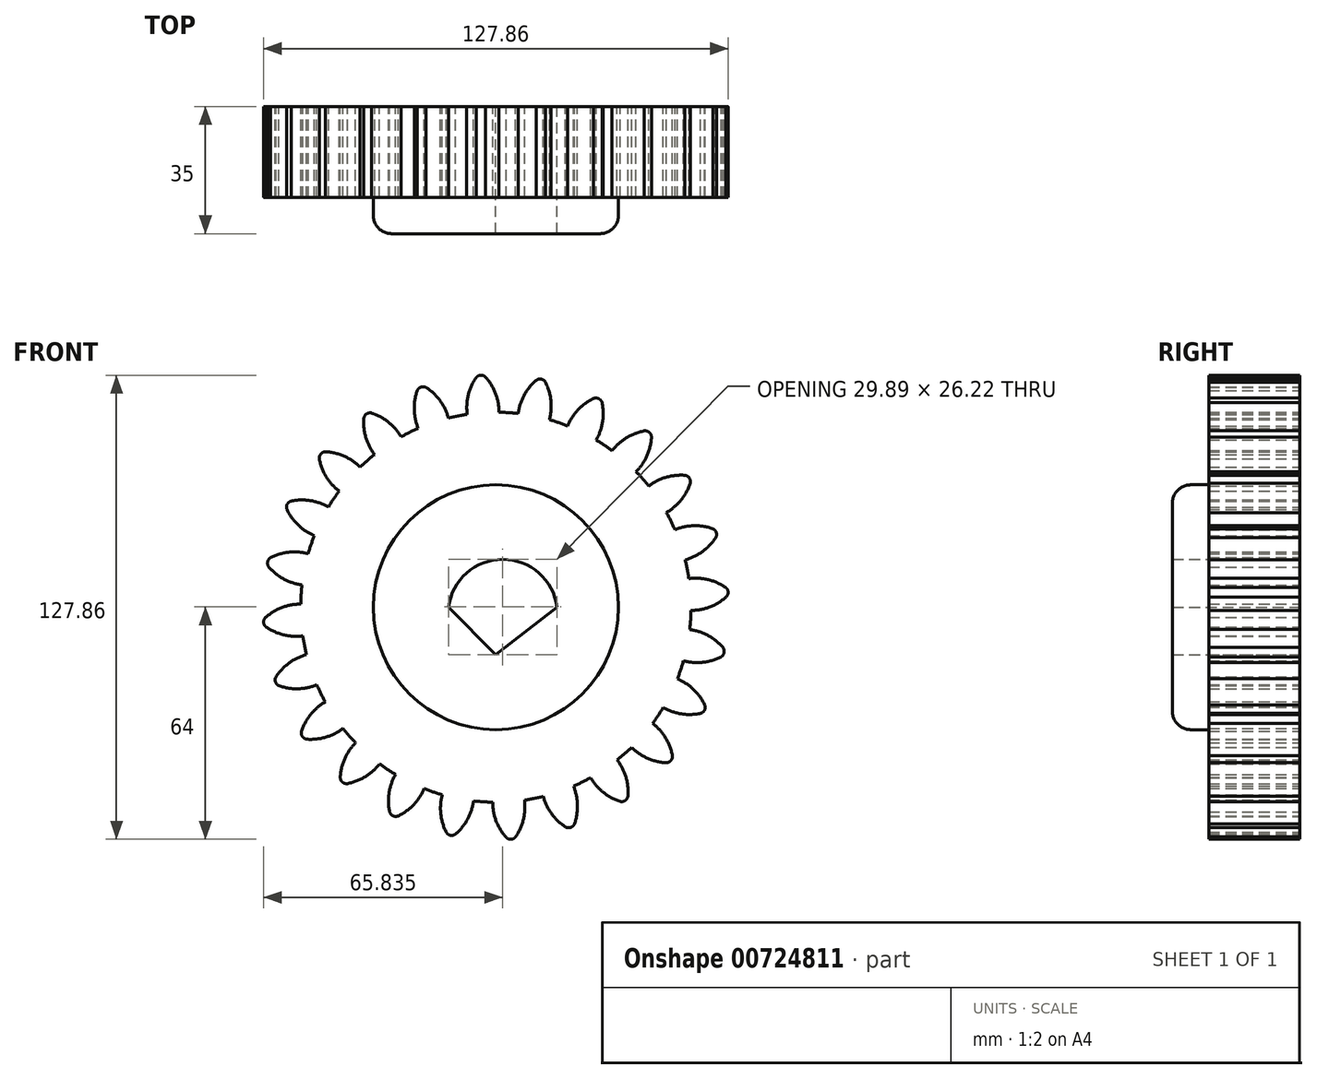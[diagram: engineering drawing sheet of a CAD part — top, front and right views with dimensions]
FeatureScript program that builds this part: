
annotation { "Feature Type Name" : "Feature", "Feature Type Description" : "" }
export const myFeature = defineFeature(function(context is Context, id is Id, definition is map)
    precondition{}
    {
        {
            var Q0;
            Q0=qCreatedBy(makeId("Front.planeOp"),FACE);
            var sketch = newSketch(context, id + "F0", { "sketchPlane" : qUnion([Q0])});
            skCircle(sketch, "E0", {"center": v(0, 0) * mm, "radius": 63.5 * mm, "construction": true});
            skCircle(sketch, "E1", {"center": v(0, 0) * mm, "radius": 58.67 * mm, "construction": true});
            skCircle(sketch, "E2", {"center": v(0, 0) * mm, "radius": 53.72 * mm});
            skLineSegment(sketch, "E3", {"start": v(0, 0) * mm, "end": v(0, 81.95) * mm, "construction": true});
            skLineSegment(sketch, "E4", {"start": v(0, 81.95) * mm, "end": v(0, 0) * mm, "construction": true});
            skLineSegment(sketch, "E5", {"start": v(0, 0) * mm, "end": v(-5.35, 81.6) * mm, "construction": true});
            skLineSegment(sketch, "E6", {"start": v(0, 58.67) * mm, "end": v(-69.28, 58.67) * mm, "construction": true});
            skLineSegment(sketch, "E7", {"start": v(0, 58.67) * mm, "end": v(-66.67, 34.4) * mm, "construction": true});
            skCircle(sketch, "E8", {"center": v(0, 0) * mm, "radius": 55.14 * mm, "construction": true});
            skCircle(sketch, "E9", {"center": v(0, 58.67) * mm, "radius": 14.6 * mm, "construction": true});
            skCircle(sketch, "E10", {"center": v(-13.72, 53.68) * mm, "radius": 14.6 * mm, "construction": true});
            skArc(sketch, "E11", {"start": v(0, 58.67) * mm, "mid": v(-1.2, 61.2) * mm, "end": v(-2.86, 63.44) * mm});
            skArc(sketch, "E12", {"start": v(0.88, 53.71) * mm, "mid": v(0.65, 56.23) * mm, "end": v(0, 58.67) * mm});
            skArc(sketch, "E13.MirrorCS", {"start": v(-7.66, 58.17) * mm, "mid": v(-6.8, 60.82) * mm, "end": v(-5.45, 63.27) * mm});
            skArc(sketch, "E14.MirrorCS", {"start": v(-7.88, 53.14) * mm, "mid": v(-7.99, 55.67) * mm, "end": v(-7.66, 58.17) * mm});
            skArc(sketch, "E15", {"start": v(-2.86, 63.44) * mm, "mid": v(-4.2, 63.93) * mm, "end": v(-5.45, 63.27) * mm});
            skSolve(sketch);
        }
        {
            var Q0;
            {var subQ0=sQuery(id+"F0.wireOp",EDGE,"E2");var subQ1=makeQuery(id+"F0.imprint","INTERSECT",VERTEX,{"derivedFrom":[subQ0,sQuery(id+"F0.wireOp",EDGE,"E12")]});Q0=makeQuery(id+"F0.imprint","IMPRINT",FACE,{"disambiguationData":[TD([[makeQuery(id+"F0.imprint","IMPRINT",EDGE,{"disambiguationData":[TD([[subQ1,-1.0]])],"derivedFrom":subQ0}),1.0]])]});}
            var Q1;
            Q1=makeQuery(id+"F0.imprint","IMPRINT",FACE,{"disambiguationData":[TD([[makeQuery(id+"F0.imprint","IMPRINT",EDGE,{"derivedFrom":sQuery(id+"F0.wireOp",EDGE,"E11")}),1.0]])]});
            extrude(context, id + "F1", {"entities" : qUnion([Q0, Q1]), "depth" : 25 * mm, "offsetDistance" : 25 * mm});
        }
        {
            var Q0;
            Q0=makeQuery(id+"F1.opExtrude","SWEPT_BODY",BODY,{"disambiguationData":[OSD([sQuery(id+"F0.wireOp",EDGE,"E2"),sQuery(id+"F0.wireOp",EDGE,"E11"),sQuery(id+"F0.wireOp",EDGE,"E12"),sQuery(id+"F0.wireOp",EDGE,"E13.MirrorCS"),sQuery(id+"F0.wireOp",EDGE,"E14.MirrorCS"),sQuery(id+"F0.wireOp",EDGE,"E15")])]});
            var Q1;
            Q1=makeQuery(id+"F1.opExtrude","SWEPT_FACE",FACE,{"disambiguationData":[OSD([sQuery(id+"F0.wireOp",EDGE,"E2")])]});
            circularPattern(context, id + "F2", {"operationType" : NewBodyOperationType.ADD, "entities" : qUnion([Q0]), "axis" : qUnion([Q1]), "angle" : 360 * degree, "instanceCount" : 24, "equalSpace" : true});
        }
        {
            var Q0;
            {var subQ0=makeQuery(id+"F1.opExtrude","CAP_FACE",FACE,{"disambiguationData":[OSD([sQuery(id+"F0.wireOp",EDGE,"E2"),sQuery(id+"F0.wireOp",EDGE,"E11"),sQuery(id+"F0.wireOp",EDGE,"E12"),sQuery(id+"F0.wireOp",EDGE,"E13.MirrorCS"),sQuery(id+"F0.wireOp",EDGE,"E14.MirrorCS"),sQuery(id+"F0.wireOp",EDGE,"E15")])],"isStart":false});Q0=makeQuery(id+"F2.boolean.opBoolean","MERGE",FACE,{"derivedFrom":[subQ0,makeQuery(id+"F2.opPattern","COPY",FACE,{"derivedFrom":subQ0,"instanceName":"1"}),makeQuery(id+"F2.opPattern","COPY",FACE,{"derivedFrom":subQ0,"instanceName":"2"}),makeQuery(id+"F2.opPattern","COPY",FACE,{"derivedFrom":subQ0,"instanceName":"3"}),makeQuery(id+"F2.opPattern","COPY",FACE,{"derivedFrom":subQ0,"instanceName":"4"}),makeQuery(id+"F2.opPattern","COPY",FACE,{"derivedFrom":subQ0,"instanceName":"5"}),makeQuery(id+"F2.opPattern","COPY",FACE,{"derivedFrom":subQ0,"instanceName":"6"}),makeQuery(id+"F2.opPattern","COPY",FACE,{"derivedFrom":subQ0,"instanceName":"7"}),makeQuery(id+"F2.opPattern","COPY",FACE,{"derivedFrom":subQ0,"instanceName":"8"}),makeQuery(id+"F2.opPattern","COPY",FACE,{"derivedFrom":subQ0,"instanceName":"9"}),makeQuery(id+"F2.opPattern","COPY",FACE,{"derivedFrom":subQ0,"instanceName":"10"}),makeQuery(id+"F2.opPattern","COPY",FACE,{"derivedFrom":subQ0,"instanceName":"11"}),makeQuery(id+"F2.opPattern","COPY",FACE,{"derivedFrom":subQ0,"instanceName":"12"}),makeQuery(id+"F2.opPattern","COPY",FACE,{"derivedFrom":subQ0,"instanceName":"13"}),makeQuery(id+"F2.opPattern","COPY",FACE,{"derivedFrom":subQ0,"instanceName":"14"}),makeQuery(id+"F2.opPattern","COPY",FACE,{"derivedFrom":subQ0,"instanceName":"15"}),makeQuery(id+"F2.opPattern","COPY",FACE,{"derivedFrom":subQ0,"instanceName":"16"}),makeQuery(id+"F2.opPattern","COPY",FACE,{"derivedFrom":subQ0,"instanceName":"17"}),makeQuery(id+"F2.opPattern","COPY",FACE,{"derivedFrom":subQ0,"instanceName":"18"}),makeQuery(id+"F2.opPattern","COPY",FACE,{"derivedFrom":subQ0,"instanceName":"19"}),makeQuery(id+"F2.opPattern","COPY",FACE,{"derivedFrom":subQ0,"instanceName":"20"}),makeQuery(id+"F2.opPattern","COPY",FACE,{"derivedFrom":subQ0,"instanceName":"21"}),makeQuery(id+"F2.opPattern","COPY",FACE,{"derivedFrom":subQ0,"instanceName":"22"}),makeQuery(id+"F2.opPattern","COPY",FACE,{"derivedFrom":subQ0,"instanceName":"23"})]});}
            var sketch = newSketch(context, id + "F3", { "sketchPlane" : qUnion([Q0])});
            skArc(sketch, "E16", {"start": v(16.85, 0) * mm, "mid": v(1.9, 13.18) * mm, "end": v(-13.04, 0) * mm});
            skLineSegment(sketch, "E17", {"start": v(-13.04, 0) * mm, "end": v(0, -13.04) * mm});
            skLineSegment(sketch, "E18", {"start": v(0, -13.04) * mm, "end": v(16.85, 0) * mm});
            skCircle(sketch, "E19", {"center": v(0, 0) * mm, "radius": 33.72 * mm});
            skSolve(sketch);
        }
        {
            var Q0;
            Q0=makeQuery(id+"F3.imprint","IMPRINT",FACE,{"disambiguationData":[TD([[makeQuery(id+"F3.imprint","IMPRINT",EDGE,{"derivedFrom":sQuery(id+"F3.wireOp",EDGE,"E16")}),-1.0]])]});
            extrude(context, id + "F4", {"entities" : qUnion([Q0]), "operationType" : NewBodyOperationType.ADD, "endBound" : BoundingType.SYMMETRIC, "depth" : 20 * mm, "offsetDistance" : 25 * mm});
        }
        {
            var Q0;
            {var subQ0=makeQuery(id+"F1.opExtrude","CAP_FACE",FACE,{"disambiguationData":[OSD([sQuery(id+"F0.wireOp",EDGE,"E2"),sQuery(id+"F0.wireOp",EDGE,"E11"),sQuery(id+"F0.wireOp",EDGE,"E12"),sQuery(id+"F0.wireOp",EDGE,"E13.MirrorCS"),sQuery(id+"F0.wireOp",EDGE,"E14.MirrorCS"),sQuery(id+"F0.wireOp",EDGE,"E15")])],"isStart":false});Q0=makeQuery(id+"F4.boolean.opBoolean","SPLIT",FACE,{"disambiguationData":[TD([makeQuery(id+"F4.opExtrude","SWEPT_FACE",FACE,{"disambiguationData":[OSD([sQuery(id+"F3.wireOp",EDGE,"E16")])]})])],"derivedFrom":makeQuery(id+"F2.boolean.opBoolean","MERGE",FACE,{"derivedFrom":[subQ0,makeQuery(id+"F2.opPattern","COPY",FACE,{"derivedFrom":subQ0,"instanceName":"1"}),makeQuery(id+"F2.opPattern","COPY",FACE,{"derivedFrom":subQ0,"instanceName":"2"}),makeQuery(id+"F2.opPattern","COPY",FACE,{"derivedFrom":subQ0,"instanceName":"3"}),makeQuery(id+"F2.opPattern","COPY",FACE,{"derivedFrom":subQ0,"instanceName":"4"}),makeQuery(id+"F2.opPattern","COPY",FACE,{"derivedFrom":subQ0,"instanceName":"5"}),makeQuery(id+"F2.opPattern","COPY",FACE,{"derivedFrom":subQ0,"instanceName":"6"}),makeQuery(id+"F2.opPattern","COPY",FACE,{"derivedFrom":subQ0,"instanceName":"7"}),makeQuery(id+"F2.opPattern","COPY",FACE,{"derivedFrom":subQ0,"instanceName":"8"}),makeQuery(id+"F2.opPattern","COPY",FACE,{"derivedFrom":subQ0,"instanceName":"9"}),makeQuery(id+"F2.opPattern","COPY",FACE,{"derivedFrom":subQ0,"instanceName":"10"}),makeQuery(id+"F2.opPattern","COPY",FACE,{"derivedFrom":subQ0,"instanceName":"11"}),makeQuery(id+"F2.opPattern","COPY",FACE,{"derivedFrom":subQ0,"instanceName":"12"}),makeQuery(id+"F2.opPattern","COPY",FACE,{"derivedFrom":subQ0,"instanceName":"13"}),makeQuery(id+"F2.opPattern","COPY",FACE,{"derivedFrom":subQ0,"instanceName":"14"}),makeQuery(id+"F2.opPattern","COPY",FACE,{"derivedFrom":subQ0,"instanceName":"15"}),makeQuery(id+"F2.opPattern","COPY",FACE,{"derivedFrom":subQ0,"instanceName":"16"}),makeQuery(id+"F2.opPattern","COPY",FACE,{"derivedFrom":subQ0,"instanceName":"17"}),makeQuery(id+"F2.opPattern","COPY",FACE,{"derivedFrom":subQ0,"instanceName":"18"}),makeQuery(id+"F2.opPattern","COPY",FACE,{"derivedFrom":subQ0,"instanceName":"19"}),makeQuery(id+"F2.opPattern","COPY",FACE,{"derivedFrom":subQ0,"instanceName":"20"}),makeQuery(id+"F2.opPattern","COPY",FACE,{"derivedFrom":subQ0,"instanceName":"21"}),makeQuery(id+"F2.opPattern","COPY",FACE,{"derivedFrom":subQ0,"instanceName":"22"}),makeQuery(id+"F2.opPattern","COPY",FACE,{"derivedFrom":subQ0,"instanceName":"23"})]})});}
            extrude(context, id + "F5", {"entities" : qUnion([Q0]), "operationType" : NewBodyOperationType.REMOVE, "endBound" : BoundingType.SYMMETRIC, "oppositeDirection" : true, "depth" : 50 * mm, "offsetDistance" : 25 * mm});
        }
        {
            var Q0;
            Q0=makeQuery(id+"F4.opExtrude","CAP_EDGE",EDGE,{"disambiguationData":[OSD([sQuery(id+"F3.wireOp",EDGE,"E19")])],"isStart":false});
            fillet(context, id + "F6", {"entities" : qUnion([Q0]), "radius" : 5 * mm, "tangentPropagation" : true, "allowEdgeOverflow" : false});
        }
    });
